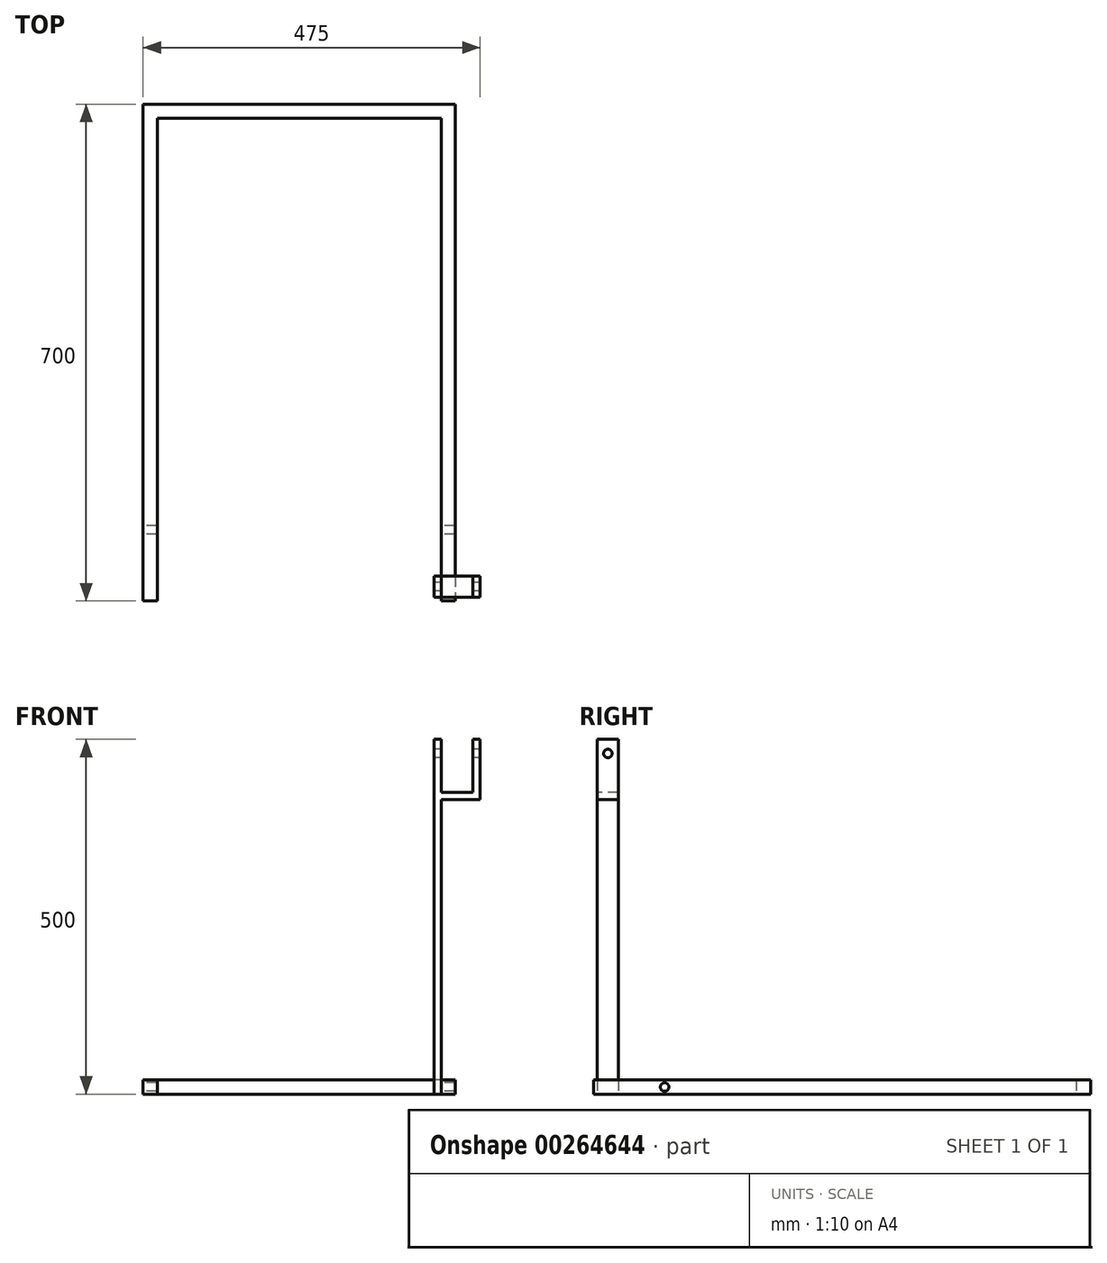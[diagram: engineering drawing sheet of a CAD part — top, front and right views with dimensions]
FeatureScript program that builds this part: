
annotation { "Feature Type Name" : "Feature", "Feature Type Description" : "" }
export const myFeature = defineFeature(function(context is Context, id is Id, definition is map)
    precondition{}
    {
        {
            var Q0;
            Q0=qCreatedBy(makeId("Right.planeOp"),FACE);
            var sketch = newSketch(context, id + "F0", { "sketchPlane" : qUnion([Q0])});
            skLineSegment(sketch, "E0", {"start": v(0, 0) * mm, "end": v(0, 20) * mm});
            skLineSegment(sketch, "E1", {"start": v(0, 20) * mm, "end": v(5, 20) * mm});
            skLineSegment(sketch, "E2", {"start": v(5, 20) * mm, "end": v(5, 500) * mm});
            skLineSegment(sketch, "E3", {"start": v(5, 500) * mm, "end": v(35, 500) * mm});
            skLineSegment(sketch, "E4", {"start": v(35, 500) * mm, "end": v(35, 20) * mm});
            skLineSegment(sketch, "E5", {"start": v(35, 20) * mm, "end": v(800, 20) * mm});
            skLineSegment(sketch, "E6", {"start": v(800, 20) * mm, "end": v(800, 0) * mm});
            skLineSegment(sketch, "E7", {"start": v(800, 0) * mm, "end": v(0, 0) * mm});
            skLineSegment(sketch, "E8", {"start": v(0, 10) * mm, "end": v(800, 10) * mm, "construction": true});
            skLineSegment(sketch, "E9", {"start": v(20, 500) * mm, "end": v(20, 0) * mm, "construction": true});
            skCircle(sketch, "E10", {"center": v(100, 10) * mm, "radius": 6 * mm});
            skCircle(sketch, "E11", {"center": v(20, 480) * mm, "radius": 6 * mm});
            skSolve(sketch);
        }
        {
            var Q0;
            Q0=qCreatedBy(makeId("Top.planeOp"),FACE);
            var sketch = newSketch(context, id + "F1", { "sketchPlane" : qUnion([Q0])});
            skLineSegment(sketch, "E12", {"start": v(0, 0) * mm, "end": v(0, 700) * mm});
            skLineSegment(sketch, "E13", {"start": v(0, 700) * mm, "end": v(440, 700) * mm});
            skLineSegment(sketch, "E14", {"start": v(440, 700) * mm, "end": v(440, 35) * mm});
            skLineSegment(sketch, "E15", {"start": v(440, 35) * mm, "end": v(520.75, 35) * mm});
            skLineSegment(sketch, "E16", {"start": v(520.75, 35) * mm, "end": v(520.75, 5) * mm});
            skLineSegment(sketch, "E17", {"start": v(520.75, 5) * mm, "end": v(440, 5) * mm});
            skLineSegment(sketch, "E18", {"start": v(440, 5) * mm, "end": v(440, 0) * mm});
            skLineSegment(sketch, "E19", {"start": v(440, 0) * mm, "end": v(420, 0) * mm});
            skLineSegment(sketch, "E20", {"start": v(420, 0) * mm, "end": v(420, 5) * mm});
            skLineSegment(sketch, "E21", {"start": v(420, 5) * mm, "end": v(410, 5) * mm});
            skLineSegment(sketch, "E22", {"start": v(410, 5) * mm, "end": v(410, 35) * mm});
            skLineSegment(sketch, "E23", {"start": v(410, 35) * mm, "end": v(420, 35) * mm});
            skLineSegment(sketch, "E24", {"start": v(420, 35) * mm, "end": v(420, 680) * mm});
            skLineSegment(sketch, "E25", {"start": v(420, 680) * mm, "end": v(20, 680) * mm});
            skLineSegment(sketch, "E26", {"start": v(20, 680) * mm, "end": v(20, 0) * mm});
            skLineSegment(sketch, "E27", {"start": v(20, 0) * mm, "end": v(0, 0) * mm});
            skSolve(sketch);
        }
        {
            var Q0;
            Q0=makeQuery(id+"F1.imprint","IMPRINT",FACE,{"disambiguationData":[TD([[makeQuery(id+"F1.imprint","IMPRINT",EDGE,{"derivedFrom":sQuery(id+"F1.wireOp",EDGE,"E12")}),-1.0]])]});
            extrude(context, id + "F2", {"entities" : qUnion([Q0]), "depth" : 926 * mm});
        }
        {
            var Q0;
            Q0 = qSketchRegion(id + "F0", true);
            extrude(context, id + "F3", {"entities" : qUnion([Q0]), "operationType" : NewBodyOperationType.INTERSECT, "endBound" : BoundingType.SYMMETRIC, "depth" : 1188 * mm});
        }
        {
            var Q0;
            Q0=qCreatedBy(makeId("Front.planeOp"),FACE);
            var sketch = newSketch(context, id + "F4", { "sketchPlane" : qUnion([Q0])});
            skLineSegment(sketch, "E28", {"start": v(0, 0) * mm, "end": v(0, 20) * mm});
            skLineSegment(sketch, "E29", {"start": v(0, 20) * mm, "end": v(410, 20) * mm});
            skLineSegment(sketch, "E30", {"start": v(410, 20) * mm, "end": v(410, 520) * mm});
            skLineSegment(sketch, "E31", {"start": v(410, 520) * mm, "end": v(420, 520) * mm});
            skLineSegment(sketch, "E32", {"start": v(420, 520) * mm, "end": v(420, 425) * mm});
            skLineSegment(sketch, "E33", {"start": v(420, 425) * mm, "end": v(465, 425) * mm});
            skLineSegment(sketch, "E34", {"start": v(465, 425) * mm, "end": v(465, 520) * mm});
            skLineSegment(sketch, "E35", {"start": v(465, 520) * mm, "end": v(475, 520) * mm});
            skLineSegment(sketch, "E36", {"start": v(475, 520) * mm, "end": v(475, 415) * mm});
            skLineSegment(sketch, "E37", {"start": v(475, 415) * mm, "end": v(420, 415) * mm});
            skLineSegment(sketch, "E38", {"start": v(420, 415) * mm, "end": v(420, 20) * mm});
            skLineSegment(sketch, "E39", {"start": v(440, 0) * mm, "end": v(0, 0) * mm});
            skLineSegment(sketch, "E40", {"start": v(420, 20) * mm, "end": v(440, 20) * mm});
            skLineSegment(sketch, "E41", {"start": v(440, 20) * mm, "end": v(440, 0) * mm});
            skSolve(sketch);
        }
        {
            var Q0;
            Q0 = qSketchRegion(id + "F4", true);
            extrude(context, id + "F5", {"entities" : qUnion([Q0]), "operationType" : NewBodyOperationType.INTERSECT, "oppositeDirection" : true, "depth" : 769 * mm});
        }
    });
